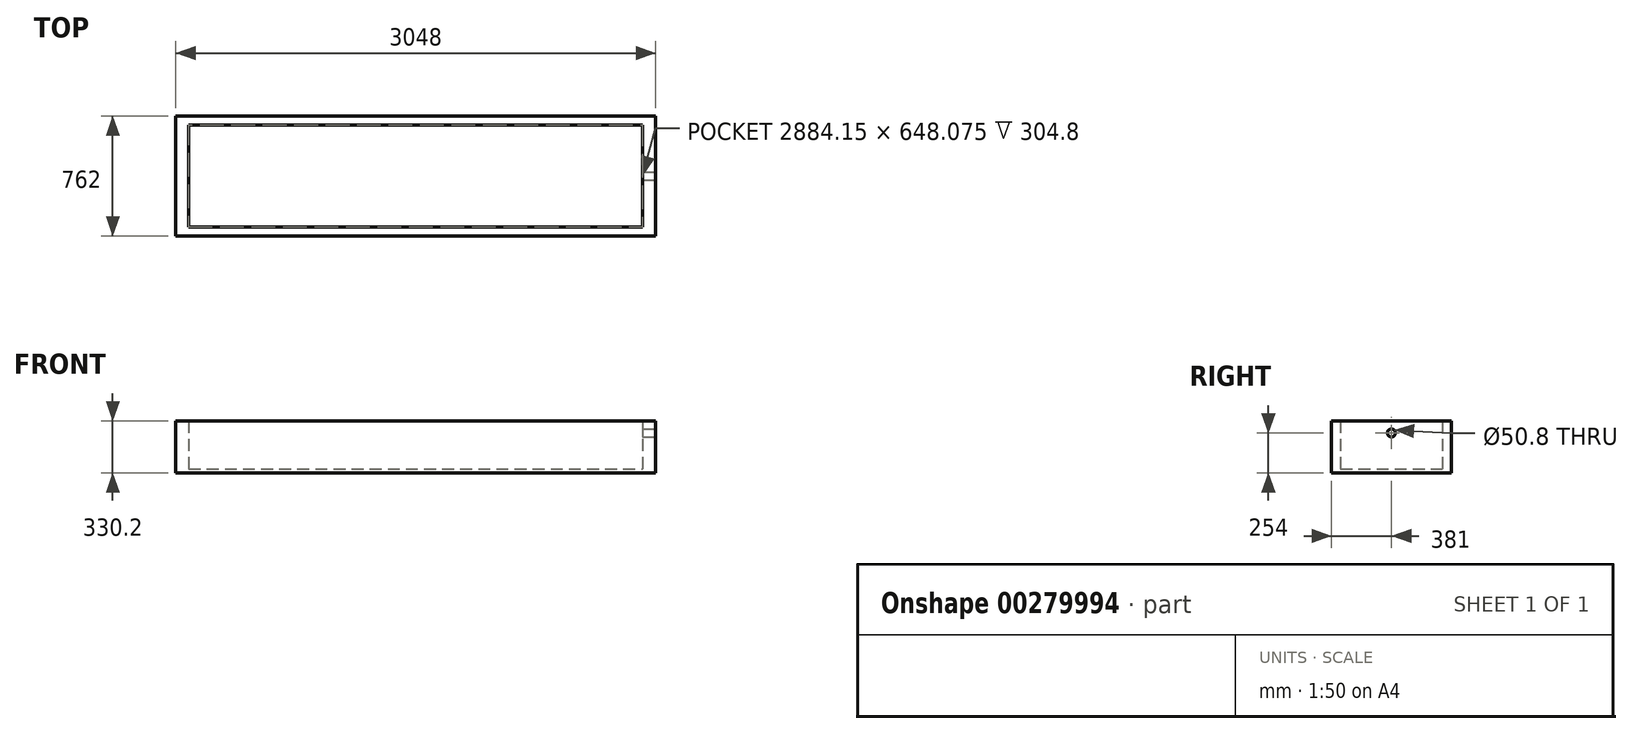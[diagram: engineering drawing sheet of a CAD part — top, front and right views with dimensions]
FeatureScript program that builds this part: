
annotation { "Feature Type Name" : "Feature", "Feature Type Description" : "" }
export const myFeature = defineFeature(function(context is Context, id is Id, definition is map)
    precondition{}
    {
        {
            var Q0;
            Q0=qCreatedBy(makeId("Top.planeOp"),FACE);
            var sketch = newSketch(context, id + "F0", { "sketchPlane" : qUnion([Q0])});
            skLineSegment(sketch, "E0.bottom", {"start": v(1524, 381) * mm, "end": v(-1524, 381) * mm});
            skLineSegment(sketch, "E0.top", {"start": v(1524, -381) * mm, "end": v(-1524, -381) * mm});
            skLineSegment(sketch, "E0.left", {"start": v(1524, 381) * mm, "end": v(1524, -381) * mm});
            skLineSegment(sketch, "E0.right", {"start": v(-1524, 381) * mm, "end": v(-1524, -381) * mm});
            skPoint(sketch, "E0.middle", {"position": v(0, 0) * mm});
            skLineSegment(sketch, "E1.bottom", {"start": v(-1442.08, -324.04) * mm, "end": v(1442.08, -324.04) * mm});
            skLineSegment(sketch, "E1.top", {"start": v(-1442.08, 324.04) * mm, "end": v(1442.08, 324.04) * mm});
            skLineSegment(sketch, "E1.left", {"start": v(-1442.08, -324.04) * mm, "end": v(-1442.08, 324.04) * mm});
            skLineSegment(sketch, "E1.right", {"start": v(1442.08, -324.04) * mm, "end": v(1442.08, 324.04) * mm});
            skSolve(sketch);
        }
        {
            var Q0;
            Q0=makeQuery(id+"F0.imprint","IMPRINT",FACE,{"disambiguationData":[TD([[makeQuery(id+"F0.imprint","IMPRINT",EDGE,{"derivedFrom":sQuery(id+"F0.wireOp",EDGE,"E1.bottom")}),1.0]])]});
            var Q1;
            Q1=makeQuery(id+"F0.imprint","IMPRINT",FACE,{"disambiguationData":[TD([[makeQuery(id+"F0.imprint","IMPRINT",EDGE,{"derivedFrom":sQuery(id+"F0.wireOp",EDGE,"E0.bottom")}),1.0]])]});
            extrude(context, id + "F1", {"entities" : qUnion([Q0, Q1]), "oppositeDirection" : true, "depth" : 25.4 * mm});
        }
        {
            var Q0;
            Q0 = qSketchRegion(id + "F0", true);
            extrude(context, id + "F2", {"entities" : qUnion([Q0]), "operationType" : NewBodyOperationType.ADD, "depth" : 304.8 * mm});
        }
        {
            var Q0;
            {var subQ0=sQuery(id+"F0.wireOp",EDGE,"E0.left");Q0=makeQuery(id+"F2.boolean.opBoolean","MERGE",FACE,{"derivedFrom":[makeQuery(id+"F1.opExtrude","SWEPT_FACE",FACE,{"disambiguationData":[OSD([subQ0])]}),makeQuery(id+"F2.opExtrude","SWEPT_FACE",FACE,{"disambiguationData":[OSD([subQ0])]})]});}
            var sketch = newSketch(context, id + "F3", { "sketchPlane" : qUnion([Q0])});
            skCircle(sketch, "E2", {"center": v(0, 228.6) * mm, "radius": 25.4 * mm});
            skSolve(sketch);
        }
        {
            var Q0;
            Q0=makeQuery(id+"F3.imprint","IMPRINT",FACE,{"disambiguationData":[TD([[makeQuery(id+"F3.imprint","IMPRINT",EDGE,{"derivedFrom":sQuery(id+"F3.wireOp",EDGE,"E2")}),1.0]])]});
            extrude(context, id + "F4", {"entities" : qUnion([Q0]), "operationType" : NewBodyOperationType.REMOVE, "endBound" : BoundingType.UP_TO_NEXT, "oppositeDirection" : true, "depth" : 25.4 * mm});
        }
    });
